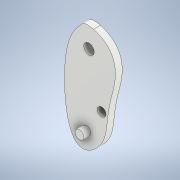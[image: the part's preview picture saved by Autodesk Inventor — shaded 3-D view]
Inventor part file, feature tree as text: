
AUTODESK INVENTOR PART (.ipt)
format: ipt  version: 2022 (Build 260153000, 153)  size: 136,192 bytes
history: native  units: in
note: dims shown in document units (in); Inventor stores cm internally (conversion verified against a paired STEP export)
features: extrude x3, sketch x2, projected_geometry x1
ambient origin geometry x8: Origin, YZ Plane, XZ Plane, XY Plane, X Axis, Y Axis, Z Axis, Center Point
bodies: Solid1 (feature_tree)
feature tree (6):
  sketch  "Sketch2"  dims[d0=0.1969in d1=0.0in d2=0.1969in d3=0.0in]
  extrude  "Extrusion1"  Depth=0.1969in TaperAngle=0.0deg
  extrude  "Extrusion2"  [1 undecoded]
  extrude  "Extrusion3"  [1 undecoded]
  sketch  "Sketch3"  dims[d4=0.1969in d5=0.0in]
  projected_geometry  "Projected Loop2"
note: 2 required parameter values undecoded (feature->parameter linkage not recoverable at this tier; creation-order binding heuristic only, values carry confidence <= 0.55)
